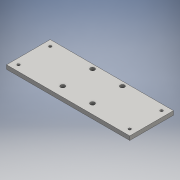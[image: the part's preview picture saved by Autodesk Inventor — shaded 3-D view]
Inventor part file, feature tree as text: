
AUTODESK INVENTOR PART (.ipt)
format: ipt  version: 2016 (Build 200138000, 138)  size: 122,368 bytes
history: native  units: mm
features: sketch x3, hole x2, extrude x1
ambient origin geometry x8: Origin, YZ Plane, XZ Plane, XY Plane, X Axis, Y Axis, Z Axis, Center Point
bodies: Solid1 (feature_tree)
feature tree (6):
  extrude  "Extrusion1"  Depth=310.0mm
  hole  "Hole1"  [1 undecoded]
  hole  "Hole2"  [1 undecoded]
  sketch  "Sketch1"  dims[d0=110.0mm d1=310.0mm]
  sketch  "Sketch2"  dims[d2=155.0mm d3=55.0mm]
  sketch  "Sketch3"  dims[d4=10.0mm d5=0.0mm d6=75.0mm d7=11.0mm d8=75.0mm d9=6.6mm d10=6.0mm d11=11.0mm d12=7.0mm d13=14.3117mm d14=8.0mm d15=20.594885mm d16=80.0mm d17=40.0mm d18=280.0mm d19=140.0mm d20=6.6mm d21=6.0mm d22=11.0mm d23=7.0mm d24=14.3117mm d25=8.0mm d26=20.594885mm d27=37.5mm]
note: 2 required parameter values undecoded (feature->parameter linkage not recoverable at this tier; creation-order binding heuristic only, values carry confidence <= 0.55)
